# Revit family: 70279
name_source: partatom
category: Luminarias
revit_build: Autodesk Revit 2018 (Build: 20170223_1515(x64)
units: mm (PartAtom-declared; Revit-internal decimal feet)

## family parameters
Compartido = No
Corte con vacíos al cargar = Sí
Cota de conector redondo = Diámetro de uso
Número OmniClass = 23.80.70.00
Origen de luz = No
Punto de cálculo de habitación = No
Se basa en plano de trabajo = Sí
Siempre vertical = No
Tipo de pieza = Normal
Título OmniClass = Lighting

## types (2) — shared parameters
Elevación por defecto = 1219 mm
FARO_Category = Accessories
FARO_Last Actualization Date = 23/06/2020
FARO_Model Line = DART
FARO_URL Model = https://faro.es
Fabricante = FARO Barcelona
URL = https://www.faro.es

## per-type parameters (varying)
| type | FARO_Description EN | FARO_EAN | FARO_Ref |
| 70280 Surface black box DART-2 | Surface black box DART-2 | 8421776183438 | 70280 |
| 70279 Surface White box DART-2 | Surface White box DART-2 | 8421776183421 | 70279 |

## geometry (parser evidence)
native form markers: Sweep x3
no freeform markers — native parametric forms only
